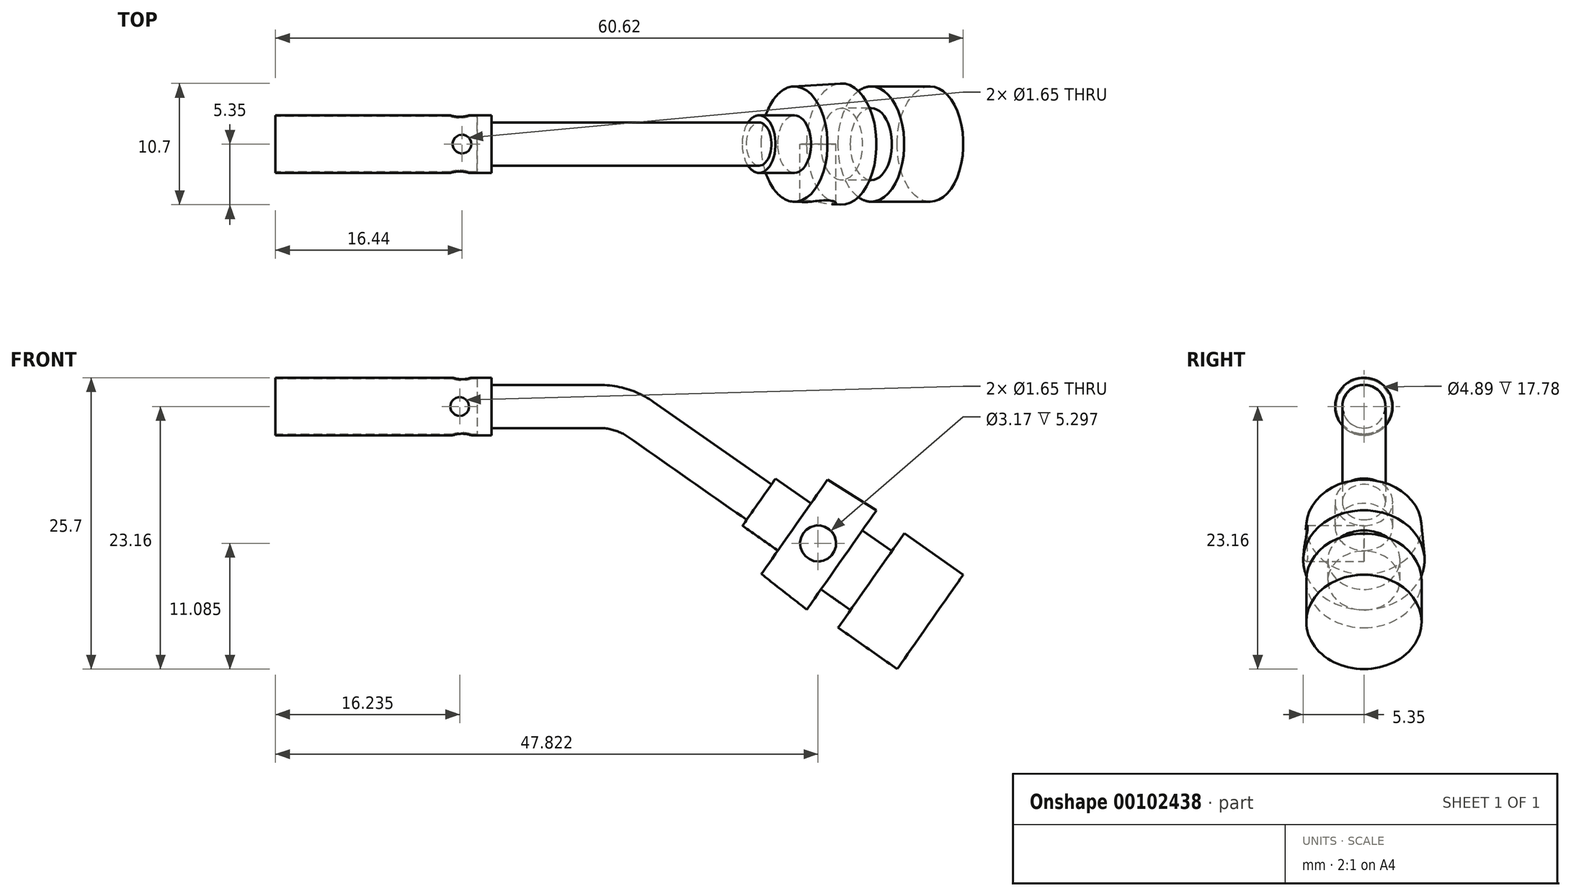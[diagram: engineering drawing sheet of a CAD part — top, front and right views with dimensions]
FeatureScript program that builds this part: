
annotation { "Feature Type Name" : "Feature", "Feature Type Description" : "" }
export const myFeature = defineFeature(function(context is Context, id is Id, definition is map)
    precondition{}
    {
        {
            var Q0;
            Q0=qCreatedBy(makeId("Right.planeOp"),FACE);
            var sketch = newSketch(context, id + "F0", { "sketchPlane" : qUnion([Q0])});
            skCircle(sketch, "E0", {"center": v(0, 0) * mm, "radius": 2.54 * mm});
            skSolve(sketch);
        }
        {
            var Q0;
            Q0=makeQuery(id+"F0.imprint","IMPRINT",FACE,{"disambiguationData":[TD([[makeQuery(id+"F0.imprint","IMPRINT",EDGE,{"derivedFrom":sQuery(id+"F0.wireOp",EDGE,"E0")}),1.0]])]});
            extrude(context, id + "F1", {"entities" : qUnion([Q0]), "depth" : 19.05 * mm});
        }
        {
            var Q0;
            Q0=makeQuery(id+"F1.opExtrude","CAP_FACE",FACE,{"disambiguationData":[OSD([sQuery(id+"F0.wireOp",EDGE,"E0")])],"isStart":false});
            var sketch = newSketch(context, id + "F2", { "sketchPlane" : qUnion([Q0])});
            skCircle(sketch, "E1", {"center": v(0, 0) * mm, "radius": 1.9 * mm});
            skSolve(sketch);
        }
        {
            var Q0;
            Q0=qCreatedBy(makeId("Front.planeOp"),FACE);
            var sketch = newSketch(context, id + "F3", { "sketchPlane" : qUnion([Q0])});
            skLineSegment(sketch, "E2.0", {"start": v(19.05, 2.54) * mm, "end": v(19.05, -2.54) * mm, "construction": true});
            skLineSegment(sketch, "E3", {"start": v(19.05, 0) * mm, "end": v(28.58, 0) * mm});
            skArc(sketch, "E4", {"start": v(32.22, -1.15) * mm, "mid": v(30.48, -0.3) * mm, "end": v(28.58, 0) * mm});
            skLineSegment(sketch, "E5", {"start": v(32.22, -1.15) * mm, "end": v(42.62, -8.43) * mm});
            skSolve(sketch);
        }
        {
            var Q0;
            Q0=makeQuery(id+"F2.imprint","IMPRINT",FACE,{"disambiguationData":[TD([[makeQuery(id+"F2.imprint","IMPRINT",EDGE,{"derivedFrom":sQuery(id+"F2.wireOp",EDGE,"E1")}),1.0]])]});
            var Q1;
            Q1=sQuery(id+"F3.wireOp",EDGE,"E3");
            var Q2;
            Q2=sQuery(id+"F3.wireOp",EDGE,"E4");
            var Q3;
            Q3=sQuery(id+"F3.wireOp",EDGE,"E5");
            sweep(context, id + "F4", {"operationType" : NewBodyOperationType.ADD, "profiles" : qUnion([Q0]), "path" : qUnion([Q1, Q2, Q3])});
        }
        {
            var Q0;
            Q0=makeQuery(id+"F4.opSweep","CAP_FACE",FACE,{"disambiguationData":[OSD([sQuery(id+"F2.wireOp",EDGE,"E1"),sQuery(id+"F3.wireOp",VERTEX,"E5.end")])],"isStart":false});
            var sketch = newSketch(context, id + "F5", { "sketchPlane" : qUnion([Q0])});
            skCircle(sketch, "E6", {"center": v(0, 17.54) * mm, "radius": 2.54 * mm});
            skSolve(sketch);
        }
        {
            var Q0;
            Q0=makeQuery(id+"F5.imprint","IMPRINT",FACE,{"disambiguationData":[TD([[makeQuery(id+"F5.imprint","IMPRINT",EDGE,{"derivedFrom":sQuery(id+"F5.wireOp",EDGE,"E6")}),1.0]])]});
            var Q1;
            Q1=makeQuery(id+"F5.imprint","IMPRINT",FACE,{"disambiguationData":[TD([[makeQuery(id+"F5.imprint","IMPRINT",EDGE,{"derivedFrom":makeQuery(id+"F4.opSweep","CAP_EDGE",EDGE,{"disambiguationData":[OSD([sQuery(id+"F2.wireOp",EDGE,"E1"),sQuery(id+"F3.wireOp",VERTEX,"E5.end")])],"isStart":false})}),1.0]])]});
            extrude(context, id + "F6", {"entities" : qUnion([Q0, Q1]), "operationType" : NewBodyOperationType.ADD, "depth" : 3.8 * mm});
        }
        {
            var Q0;
            Q0=makeQuery(id+"F6.opExtrude","CAP_FACE",FACE,{"disambiguationData":[OSD([sQuery(id+"F5.wireOp",EDGE,"E6")])],"isStart":false});
            var sketch = newSketch(context, id + "F7", { "sketchPlane" : qUnion([Q0])});
            skCircle(sketch, "E7", {"center": v(0, 17.54) * mm, "radius": 5.08 * mm});
            skSolve(sketch);
        }
        {
            var Q0;
            Q0=makeQuery(id+"F7.imprint","IMPRINT",FACE,{"disambiguationData":[TD([[makeQuery(id+"F7.imprint","IMPRINT",EDGE,{"derivedFrom":makeQuery(id+"F6.opExtrude","CAP_EDGE",EDGE,{"disambiguationData":[OSD([sQuery(id+"F5.wireOp",EDGE,"E6")])],"isStart":false})}),1.0]])]});
            var Q1;
            Q1=makeQuery(id+"F7.imprint","IMPRINT",FACE,{"disambiguationData":[TD([[makeQuery(id+"F7.imprint","IMPRINT",EDGE,{"derivedFrom":sQuery(id+"F7.wireOp",EDGE,"E7")}),1.0]])]});
            extrude(context, id + "F8", {"entities" : qUnion([Q0, Q1]), "operationType" : NewBodyOperationType.ADD, "depth" : 5.08 * mm, "hasDraft" : true, "draftAngle" : 3 * degree});
        }
        {
            var Q0;
            Q0=makeQuery(id+"F8.opExtrude","CAP_FACE",FACE,{"disambiguationData":[OSD([sQuery(id+"F7.wireOp",EDGE,"E7")])],"isStart":false});
            var sketch = newSketch(context, id + "F9", { "sketchPlane" : qUnion([Q0])});
            skCircle(sketch, "E8", {"center": v(0, 17.54) * mm, "radius": 3.18 * mm});
            skSolve(sketch);
        }
        {
            var Q0;
            Q0=makeQuery(id+"F9.imprint","IMPRINT",FACE,{"disambiguationData":[TD([[makeQuery(id+"F9.imprint","IMPRINT",EDGE,{"derivedFrom":sQuery(id+"F9.wireOp",EDGE,"E8")}),1.0]])]});
            extrude(context, id + "F10", {"entities" : qUnion([Q0]), "operationType" : NewBodyOperationType.ADD, "depth" : 3.17 * mm});
        }
        {
            var Q0;
            Q0=makeQuery(id+"F10.opExtrude","CAP_FACE",FACE,{"disambiguationData":[OSD([sQuery(id+"F9.wireOp",EDGE,"E8")])],"isStart":false});
            var sketch = newSketch(context, id + "F11", { "sketchPlane" : qUnion([Q0])});
            skCircle(sketch, "E9", {"center": v(0, 17.54) * mm, "radius": 5.08 * mm});
            skSolve(sketch);
        }
        {
            var Q0;
            Q0=makeQuery(id+"F11.imprint","IMPRINT",FACE,{"disambiguationData":[TD([[makeQuery(id+"F11.imprint","IMPRINT",EDGE,{"derivedFrom":sQuery(id+"F11.wireOp",EDGE,"E9")}),1.0]])]});
            var Q1;
            Q1=makeQuery(id+"F11.imprint","IMPRINT",FACE,{"disambiguationData":[TD([[makeQuery(id+"F11.imprint","IMPRINT",EDGE,{"derivedFrom":makeQuery(id+"F10.opExtrude","CAP_EDGE",EDGE,{"disambiguationData":[OSD([sQuery(id+"F9.wireOp",EDGE,"E8")])],"isStart":false})}),1.0]])]});
            extrude(context, id + "F12", {"entities" : qUnion([Q0, Q1]), "operationType" : NewBodyOperationType.ADD, "depth" : 6.35 * mm});
        }
        {
            var Q0;
            Q0=makeQuery(id+"F1.opExtrude","CAP_FACE",FACE,{"disambiguationData":[OSD([sQuery(id+"F0.wireOp",EDGE,"E0")])],"isStart":true});
            var sketch = newSketch(context, id + "F13", { "sketchPlane" : qUnion([Q0])});
            skCircle(sketch, "E10", {"center": v(0, 0) * mm, "radius": 2.44 * mm});
            skSolve(sketch);
        }
        {
            var Q0;
            Q0=makeQuery(id+"F13.imprint","IMPRINT",FACE,{"disambiguationData":[TD([[makeQuery(id+"F13.imprint","IMPRINT",EDGE,{"derivedFrom":sQuery(id+"F13.wireOp",EDGE,"E10")}),1.0]])]});
            extrude(context, id + "F14", {"entities" : qUnion([Q0]), "operationType" : NewBodyOperationType.REMOVE, "oppositeDirection" : true, "depth" : 17.78 * mm});
        }
        {
            var Q0;
            Q0=qCreatedBy(makeId("Top.planeOp"),FACE);
            var sketch = newSketch(context, id + "F15", { "sketchPlane" : qUnion([Q0])});
            skLineSegment(sketch, "E11", {"start": v(0, 2.54) * mm, "end": v(18.98, 2.54) * mm, "construction": true});
            skLineSegment(sketch, "E12", {"start": v(19.05, -2.54) * mm, "end": v(0, -2.54) * mm, "construction": true});
            skCircle(sketch, "E13", {"center": v(16.44, 0) * mm, "radius": 0.83 * mm});
            skSolve(sketch);
        }
        {
            var Q0;
            Q0=makeQuery(id+"F15.imprint","IMPRINT",FACE,{"disambiguationData":[TD([[makeQuery(id+"F15.imprint","IMPRINT",EDGE,{"derivedFrom":sQuery(id+"F15.wireOp",EDGE,"E13")}),1.0]])]});
            extrude(context, id + "F16", {"entities" : qUnion([Q0]), "operationType" : NewBodyOperationType.REMOVE, "endBound" : BoundingType.THROUGH_ALL, "oppositeDirection" : true, "depth" : 25.4 * mm, "hasSecondDirection" : true, "secondDirectionBound" : SecondDirectionBoundingType.THROUGH_ALL, "secondDirectionOppositeDirection" : false, "secondDirectionDepth" : 25.4 * mm});
        }
        {
            var Q0;
            Q0=qCreatedBy(makeId("Front.planeOp"),FACE);
            var sketch = newSketch(context, id + "F17", { "sketchPlane" : qUnion([Q0])});
            skLineSegment(sketch, "E14", {"start": v(0, 2.54) * mm, "end": v(19.05, 2.54) * mm, "construction": true});
            skLineSegment(sketch, "E15", {"start": v(18.78, -2.54) * mm, "end": v(0, -2.54) * mm, "construction": true});
            skCircle(sketch, "E16", {"center": v(16.24, 0) * mm, "radius": 0.83 * mm});
            skSolve(sketch);
        }
        {
            var Q0;
            Q0=makeQuery(id+"F17.imprint","IMPRINT",FACE,{"disambiguationData":[TD([[makeQuery(id+"F17.imprint","IMPRINT",EDGE,{"derivedFrom":sQuery(id+"F17.wireOp",EDGE,"E16")}),1.0]])]});
            extrude(context, id + "F18", {"entities" : qUnion([Q0]), "operationType" : NewBodyOperationType.REMOVE, "endBound" : BoundingType.THROUGH_ALL, "oppositeDirection" : true, "depth" : 25.4 * mm, "hasSecondDirection" : true, "secondDirectionBound" : SecondDirectionBoundingType.THROUGH_ALL, "secondDirectionOppositeDirection" : false, "secondDirectionDepth" : 25.4 * mm});
        }
        {
            var Q0;
            Q0=qCreatedBy(makeId("Front.planeOp"),FACE);
            var sketch = newSketch(context, id + "F19", { "sketchPlane" : qUnion([Q0])});
            skLineSegment(sketch, "E17", {"start": v(46.84, -17.91) * mm, "end": v(42.83, -14.78) * mm, "construction": true});
            skLineSegment(sketch, "E18", {"start": v(48.66, -6.46) * mm, "end": v(52.97, -9.15) * mm, "construction": true});
            skLineSegment(sketch, "E19", {"start": v(44.83, -16.35) * mm, "end": v(50.81, -7.8) * mm, "construction": true});
            skCircle(sketch, "E20", {"center": v(47.82, -12.08) * mm, "radius": 1.59 * mm});
            skSolve(sketch);
        }
        {
            var Q0;
            Q0 = qSketchRegion(id + "F19", true);
            extrude(context, id + "F20", {"entities" : qUnion([Q0]), "operationType" : NewBodyOperationType.REMOVE, "endBound" : BoundingType.THROUGH_ALL, "depth" : 25.4 * mm});
        }
    });
